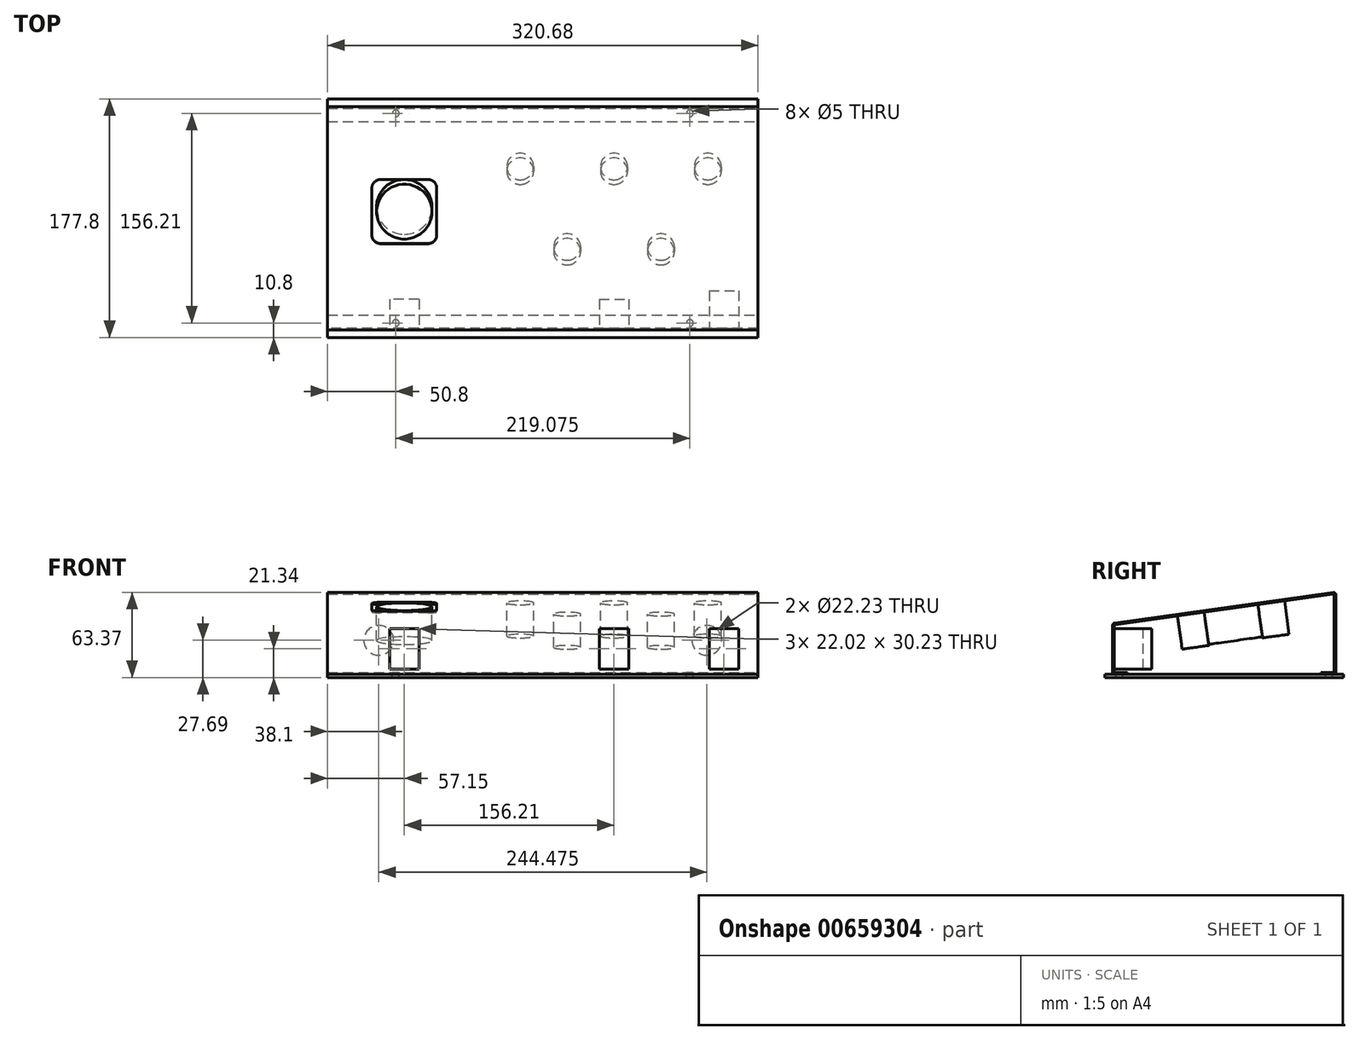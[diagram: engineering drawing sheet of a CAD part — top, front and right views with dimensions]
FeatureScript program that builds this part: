
annotation { "Feature Type Name" : "Feature", "Feature Type Description" : "" }
export const myFeature = defineFeature(function(context is Context, id is Id, definition is map)
    precondition{}
    {
        {
            var Q0;
            Q0=qCreatedBy(makeId("Front.planeOp"),FACE);
            var sketch = newSketch(context, id + "F0", { "sketchPlane" : qUnion([Q0])});
            skLineSegment(sketch, "E0.top", {"start": v(0, 38.1) * mm, "end": v(320.68, 38.1) * mm});
            skLineSegment(sketch, "E0.left", {"start": v(0, 0) * mm, "end": v(0, 38.1) * mm});
            skLineSegment(sketch, "E0.right", {"start": v(320.68, 0) * mm, "end": v(320.68, 38.1) * mm});
            skLineSegment(sketch, "E1", {"start": v(0, 0) * mm, "end": v(0, 0) * mm});
            skLineSegment(sketch, "E2", {"start": v(0, 0) * mm, "end": v(320.68, 0) * mm});
            skPoint(sketch, "E3", {"position": v(0, 19.05) * mm});
            skLineSegment(sketch, "E4.bottom", {"start": v(68.16, 3.94) * mm, "end": v(46.14, 3.94) * mm});
            skLineSegment(sketch, "E4.top", {"start": v(68.16, 34.16) * mm, "end": v(46.14, 34.16) * mm});
            skLineSegment(sketch, "E4.left", {"start": v(68.16, 3.94) * mm, "end": v(68.16, 34.16) * mm});
            skLineSegment(sketch, "E4.right", {"start": v(46.14, 3.94) * mm, "end": v(46.14, 34.16) * mm});
            skPoint(sketch, "E4.middle", {"position": v(57.15, 19.05) * mm});
            skLineSegment(sketch, "E5.bottom", {"start": v(202.35, 3.94) * mm, "end": v(224.37, 3.94) * mm});
            skLineSegment(sketch, "E5.top", {"start": v(202.35, 34.16) * mm, "end": v(224.37, 34.16) * mm});
            skLineSegment(sketch, "E5.left", {"start": v(202.35, 3.94) * mm, "end": v(202.35, 34.16) * mm});
            skLineSegment(sketch, "E5.right", {"start": v(224.37, 3.94) * mm, "end": v(224.37, 34.16) * mm});
            skPoint(sketch, "E5.middle", {"position": v(213.36, 19.05) * mm});
            skLineSegment(sketch, "E6.bottom", {"start": v(284.26, 3.94) * mm, "end": v(306.29, 3.94) * mm});
            skLineSegment(sketch, "E6.top", {"start": v(284.26, 34.16) * mm, "end": v(306.29, 34.16) * mm});
            skLineSegment(sketch, "E6.left", {"start": v(284.26, 3.94) * mm, "end": v(284.26, 34.16) * mm});
            skLineSegment(sketch, "E6.right", {"start": v(306.29, 3.94) * mm, "end": v(306.29, 34.16) * mm});
            skPoint(sketch, "E6.middle", {"position": v(295.28, 19.05) * mm});
            skSolve(sketch);
        }
        {
            var Q0;
            Q0=qCreatedBy(makeId("Right.planeOp"),FACE);
            var sketch = newSketch(context, id + "F1", { "sketchPlane" : qUnion([Q0])});
            skLineSegment(sketch, "E7.0", {"start": v(0, 0) * mm, "end": v(0, 38.1) * mm});
            skLineSegment(sketch, "E8", {"start": v(0, 0) * mm, "end": v(166.37, 0) * mm});
            skLineSegment(sketch, "E9", {"start": v(166.37, 0) * mm, "end": v(166.37, 61.34) * mm});
            skLineSegment(sketch, "E10", {"start": v(166.37, 61.34) * mm, "end": v(0, 38.1) * mm});
            skSolve(sketch);
        }
        {
            var Q0;
            Q0=sQuery(id+"F1.wireOp",EDGE,"E10");
            var Q1;
            Q1=sQuery(id+"F0.wireOp",EDGE,"E0.top");
            cPlane(context, id + "F2", {"entities" : qUnion([Q0, Q1]), "cplaneType" : CPlaneType.LINE_ANGLE, "offset" : 0 * mm, "angle" : 0 * degree, "width" : 152.4 * mm, "height" : 152.4 * mm});
        }
        {
            var Q0;
            Q0=qCreatedBy(id+"F2.planeOp",FACE);
            var sketch = newSketch(context, id + "F3", { "sketchPlane" : qUnion([Q0])});
            skPoint(sketch, "E11.0", {"position": v(320.67, 4.96) * mm});
            skPoint(sketch, "E12.0", {"position": v(0, 5.27) * mm});
            skLineSegment(sketch, "E13.bottom", {"start": v(0, 5.27) * mm, "end": v(320.68, 5.27) * mm});
            skLineSegment(sketch, "E13.top", {"start": v(0, 173.26) * mm, "end": v(320.68, 173.26) * mm});
            skLineSegment(sketch, "E13.left", {"start": v(0, 5.27) * mm, "end": v(0, 173.26) * mm});
            skLineSegment(sketch, "E13.right", {"start": v(320.68, 5.27) * mm, "end": v(320.68, 173.26) * mm});
            skCircle(sketch, "E14", {"center": v(57.15, 94.17) * mm, "radius": 20.64 * mm});
            skCircle(sketch, "E15", {"center": v(39.37, 76.4) * mm, "radius": 1.59 * mm});
            skCircle(sketch, "E16", {"center": v(74.93, 76.4) * mm, "radius": 1.59 * mm});
            skCircle(sketch, "E17", {"center": v(74.93, 111.95) * mm, "radius": 1.59 * mm});
            skCircle(sketch, "E18", {"center": v(39.37, 111.95) * mm, "radius": 1.59 * mm});
            skCircle(sketch, "E19", {"center": v(213.36, 124.42) * mm, "radius": 10 * mm});
            skCircle(sketch, "E20", {"center": v(283.21, 124.42) * mm, "radius": 10 * mm});
            skCircle(sketch, "E21", {"center": v(143.5, 124.42) * mm, "radius": 10 * mm});
            skCircle(sketch, "E22", {"center": v(178.44, 63.93) * mm, "radius": 10 * mm});
            skCircle(sketch, "E23", {"center": v(248.28, 63.93) * mm, "radius": 10 * mm});
            skLineSegment(sketch, "E24", {"start": v(178.44, 63.93) * mm, "end": v(248.28, 63.93) * mm});
            skLineSegment(sketch, "E25", {"start": v(213.36, 124.42) * mm, "end": v(213.36, 63.93) * mm});
            skPoint(sketch, "E26", {"position": v(213.36, 94.17) * mm});
            skLineSegment(sketch, "E27", {"start": v(178.44, 63.93) * mm, "end": v(213.36, 124.42) * mm});
            skLineSegment(sketch, "E28", {"start": v(143.5, 124.42) * mm, "end": v(213.36, 124.42) * mm});
            skLineSegment(sketch, "E29", {"start": v(143.5, 124.42) * mm, "end": v(178.44, 63.93) * mm});
            skLineSegment(sketch, "E30", {"start": v(213.36, 124.42) * mm, "end": v(283.21, 124.42) * mm});
            skLineSegment(sketch, "E31", {"start": v(213.36, 124.42) * mm, "end": v(248.28, 63.93) * mm});
            skLineSegment(sketch, "E32", {"start": v(248.28, 63.93) * mm, "end": v(283.21, 124.42) * mm});
            skPoint(sketch, "E33.0", {"position": v(320.68, 5.27) * mm});
            skPoint(sketch, "E34.0", {"position": v(0, 173.26) * mm});
            skLineSegment(sketch, "E35.bottom", {"start": v(74.93, 118.3) * mm, "end": v(39.37, 118.3) * mm});
            skLineSegment(sketch, "E35.top", {"start": v(74.93, 70.04) * mm, "end": v(39.37, 70.04) * mm});
            skLineSegment(sketch, "E35.left", {"start": v(81.28, 111.95) * mm, "end": v(81.28, 76.4) * mm});
            skLineSegment(sketch, "E35.right", {"start": v(33.02, 111.95) * mm, "end": v(33.02, 76.4) * mm});
            skPoint(sketch, "E36.visualSharp", {"position": v(81.28, 118.3) * mm});
            skArc(sketch, "E36.filletArc", {"start": v(81.28, 111.95) * mm, "mid": v(79.42, 116.44) * mm, "end": v(74.93, 118.3) * mm});
            skPoint(sketch, "E37.visualSharp", {"position": v(33.02, 118.3) * mm});
            skArc(sketch, "E37.filletArc", {"start": v(39.37, 118.3) * mm, "mid": v(34.88, 116.44) * mm, "end": v(33.02, 111.95) * mm});
            skPoint(sketch, "E38.visualSharp", {"position": v(33.02, 70.04) * mm});
            skArc(sketch, "E38.filletArc", {"start": v(33.02, 76.4) * mm, "mid": v(34.88, 71.9) * mm, "end": v(39.37, 70.04) * mm});
            skPoint(sketch, "E39.visualSharp", {"position": v(81.28, 70.04) * mm});
            skArc(sketch, "E39.filletArc", {"start": v(74.93, 70.04) * mm, "mid": v(79.42, 71.9) * mm, "end": v(81.28, 76.4) * mm});
            skSolve(sketch);
        }
        {
            var Q0;
            Q0=sQuery(id+"F0.wireOp",EDGE,"E0.right");
            var Q1;
            Q1=sQuery(id+"F3.wireOp",EDGE,"E13.right");
            cPlane(context, id + "F4", {"entities" : qUnion([Q0, Q1]), "cplaneType" : CPlaneType.LINE_ANGLE, "offset" : 25.4 * mm, "angle" : 0 * degree, "width" : 152.4 * mm, "height" : 152.4 * mm});
        }
        {
            var Q0;
            Q0=qCreatedBy(id+"F4.planeOp",FACE);
            var sketch = newSketch(context, id + "F5", { "sketchPlane" : qUnion([Q0])});
            skLineSegment(sketch, "E40.0", {"start": v(0, 0) * mm, "end": v(0, 38.1) * mm});
            skLineSegment(sketch, "E41.0", {"start": v(0, 0) * mm, "end": v(-166.37, 0) * mm});
            skLineSegment(sketch, "E42.0", {"start": v(-166.37, 0) * mm, "end": v(-166.37, 61.34) * mm});
            skLineSegment(sketch, "E43.0", {"start": v(-166.37, 61.34) * mm, "end": v(0, 38.1) * mm});
            skLineSegment(sketch, "E44", {"start": v(-166.37, 61.34) * mm, "end": v(-166.37, 0) * mm});
            skSolve(sketch);
        }
        {
            var Q0;
            Q0=sQuery(id+"F1.wireOp",EDGE,"E9");
            var Q1;
            Q1=sQuery(id+"F3.wireOp",EDGE,"E13.top");
            cPlane(context, id + "F6", {"entities" : qUnion([Q0, Q1]), "cplaneType" : CPlaneType.LINE_ANGLE, "offset" : 25.4 * mm, "angle" : 0 * degree, "width" : 152.4 * mm, "height" : 152.4 * mm});
        }
        {
            var Q0;
            Q0=qCreatedBy(id+"F6.planeOp",FACE);
            var sketch = newSketch(context, id + "F7", { "sketchPlane" : qUnion([Q0])});
            skLineSegment(sketch, "E45.0", {"start": v(0, 0) * mm, "end": v(0, 61.34) * mm});
            skLineSegment(sketch, "E46.0", {"start": v(0, 61.34) * mm, "end": v(-320.68, 61.34) * mm});
            skLineSegment(sketch, "E47.0", {"start": v(-320.68, 0) * mm, "end": v(-320.68, 61.34) * mm});
            skLineSegment(sketch, "E48", {"start": v(-320.68, 0) * mm, "end": v(0, 0) * mm});
            skCircle(sketch, "E49", {"center": v(-282.58, 25.4) * mm, "radius": 11.11 * mm});
            skCircle(sketch, "E50", {"center": v(-38.1, 25.4) * mm, "radius": 11.11 * mm});
            skSolve(sketch);
        }
        {
            var Q0;
            Q0=qCreatedBy(makeId("Top.planeOp"),FACE);
            var sketch = newSketch(context, id + "F8", { "sketchPlane" : qUnion([Q0])});
            skLineSegment(sketch, "E51.0", {"start": v(0, 0) * mm, "end": v(0, 166.37) * mm});
            skLineSegment(sketch, "E52.0", {"start": v(0, 0) * mm, "end": v(320.68, 0) * mm});
            skLineSegment(sketch, "E53.0", {"start": v(320.68, 0) * mm, "end": v(320.68, 166.37) * mm});
            skLineSegment(sketch, "E54.0", {"start": v(320.68, 166.37) * mm, "end": v(0, 166.37) * mm});
            skCircle(sketch, "E55", {"center": v(50.8, 161.3) * mm, "radius": 2.5 * mm});
            skCircle(sketch, "E56", {"center": v(269.88, 161.3) * mm, "radius": 2.5 * mm});
            skCircle(sketch, "E57", {"center": v(50.8, 5.08) * mm, "radius": 2.5 * mm});
            skCircle(sketch, "E58", {"center": v(269.88, 5.08) * mm, "radius": 2.5 * mm});
            skLineSegment(sketch, "E59", {"start": v(0, 11.11) * mm, "end": v(320.68, 11.11) * mm});
            skLineSegment(sketch, "E60", {"start": v(0, 155.26) * mm, "end": v(320.68, 155.26) * mm});
            skSolve(sketch);
        }
        {
            var Q0;
            Q0=makeQuery(id+"F3.imprint","IMPRINT",FACE,{"disambiguationData":[TD([[makeQuery(id+"F3.imprint","IMPRINT",EDGE,{"derivedFrom":sQuery(id+"F3.wireOp",EDGE,"E13.bottom")}),1.0]])]});
            var Q1;
            {var subQ1=sQuery(id+"F3.wireOp",EDGE,"E19");var subQ7=sQuery(id+"F3.wireOp",EDGE,"E28");var subQ11=makeQuery(id+"F3.imprint","INTERSECT",VERTEX,{"derivedFrom":[subQ1,subQ7]});Q1=makeQuery(id+"F3.imprint","IMPRINT",FACE,{"disambiguationData":[TD([[makeQuery(id+"F3.imprint","IMPRINT",EDGE,{"disambiguationData":[TD([[subQ11,-1.0]])],"derivedFrom":subQ1}),-1.0]])]});}
            var Q2;
            {var subQ3=sQuery(id+"F3.wireOp",EDGE,"E19");var subQ5=sQuery(id+"F3.wireOp",EDGE,"E27");var subQ9=makeQuery(id+"F3.imprint","INTERSECT",VERTEX,{"derivedFrom":[subQ3,subQ5]});Q2=makeQuery(id+"F3.imprint","IMPRINT",FACE,{"disambiguationData":[TD([[makeQuery(id+"F3.imprint","IMPRINT",EDGE,{"disambiguationData":[TD([[subQ9,-1.0]])],"derivedFrom":subQ3}),-1.0]])]});}
            var Q3;
            {var subQ0=sQuery(id+"F3.wireOp",EDGE,"E25");var subQ3=sQuery(id+"F3.wireOp",EDGE,"E19");var subQ4=makeQuery(id+"F3.imprint","INTERSECT",VERTEX,{"derivedFrom":[subQ3,subQ0]});Q3=makeQuery(id+"F3.imprint","IMPRINT",FACE,{"disambiguationData":[TD([[makeQuery(id+"F3.imprint","IMPRINT",EDGE,{"disambiguationData":[TD([[subQ4,-1.0]])],"derivedFrom":subQ3}),-1.0]])]});}
            var Q4;
            {var subQ0=sQuery(id+"F3.wireOp",EDGE,"E30");var subQ1=sQuery(id+"F3.wireOp",EDGE,"E19");var subQ2=makeQuery(id+"F3.imprint","INTERSECT",VERTEX,{"derivedFrom":[subQ1,subQ0]});Q4=makeQuery(id+"F3.imprint","IMPRINT",FACE,{"disambiguationData":[TD([[makeQuery(id+"F3.imprint","IMPRINT",EDGE,{"disambiguationData":[TD([[subQ2,1.0]])],"derivedFrom":subQ1}),-1.0]])]});}
            var Q5;
            Q5=makeQuery(id+"F3.imprint","IMPRINT",FACE,{"disambiguationData":[TD([[makeQuery(id+"F3.imprint","IMPRINT",EDGE,{"derivedFrom":sQuery(id+"F3.wireOp",EDGE,"E14")}),-1.0]])]});
            extrude(context, id + "F9", {"entities" : qUnion([Q0, Q1, Q2, Q3, Q4, Q5]), "oppositeDirection" : true, "depth" : 1.27 * mm, "offsetDistance" : 25.4 * mm});
        }
        {
            var Q0;
            Q0=makeQuery(id+"F0.imprint","IMPRINT",FACE,{"disambiguationData":[TD([[makeQuery(id+"F0.imprint","IMPRINT",EDGE,{"derivedFrom":sQuery(id+"F0.wireOp",EDGE,"E0.top")}),-1.0]])]});
            extrude(context, id + "F10", {"entities" : qUnion([Q0]), "operationType" : NewBodyOperationType.ADD, "oppositeDirection" : true, "depth" : 1.27 * mm, "offsetDistance" : 25.4 * mm});
        }
        {
            var Q0;
            Q0=makeQuery(id+"F7.imprint","IMPRINT",FACE,{"disambiguationData":[TD([[makeQuery(id+"F7.imprint","IMPRINT",EDGE,{"derivedFrom":sQuery(id+"F7.wireOp",EDGE,"E45.0")}),1.0]])]});
            extrude(context, id + "F11", {"entities" : qUnion([Q0]), "operationType" : NewBodyOperationType.ADD, "oppositeDirection" : true, "depth" : 1.27 * mm, "offsetDistance" : 25.4 * mm});
        }
        {
            var Q0;
            Q0=makeQuery(id+"F5.imprint","IMPRINT",FACE,{"disambiguationData":[TD([[makeQuery(id+"F5.imprint","IMPRINT",EDGE,{"derivedFrom":sQuery(id+"F5.wireOp",EDGE,"E43.0")}),-1.0]])]});
            var sketch = newSketch(context, id + "F12", { "sketchPlane" : qUnion([Q0])});
            skLineSegment(sketch, "E61.0", {"start": v(-165.1, 61.34) * mm, "end": v(-166.37, 61.34) * mm});
            skLineSegment(sketch, "E62.0", {"start": v(-165.1, 61.16) * mm, "end": v(-165.1, 61.34) * mm});
            skLineSegment(sketch, "E63.0", {"start": v(-166.55, 60.08) * mm, "end": v(-166.37, 61.34) * mm});
            skLineSegment(sketch, "E64.0", {"start": v(-166.37, 60.06) * mm, "end": v(-166.55, 60.08) * mm});
            skLineSegment(sketch, "E65", {"start": v(-165.1, 61.16) * mm, "end": v(-166.37, 61.34) * mm});
            skLineSegment(sketch, "E66", {"start": v(-166.37, 60.06) * mm, "end": v(-166.37, 61.34) * mm});
            skSolve(sketch);
        }
        {
            var Q0;
            Q0=makeQuery(id+"F12.imprint","IMPRINT",FACE,{"disambiguationData":[TD([[makeQuery(id+"F12.imprint","IMPRINT",EDGE,{"derivedFrom":sQuery(id+"F12.wireOp",EDGE,"E61.0")}),1.0]])]});
            var Q1;
            Q1=makeQuery(id+"F12.imprint","IMPRINT",FACE,{"disambiguationData":[TD([[makeQuery(id+"F12.imprint","IMPRINT",EDGE,{"derivedFrom":sQuery(id+"F12.wireOp",EDGE,"E63.0")}),-1.0]])]});
            extrude(context, id + "F13", {"entities" : qUnion([Q0, Q1]), "operationType" : NewBodyOperationType.REMOVE, "endBound" : BoundingType.THROUGH_ALL, "depth" : 25.4 * mm, "offsetDistance" : 25.4 * mm});
        }
        {
            var Q0;
            {var subQ1=sQuery(id+"F8.wireOp",EDGE,"E52.0");Q0=makeQuery(id+"F8.imprint","IMPRINT",FACE,{"disambiguationData":[TD([[makeQuery(id+"F8.imprint","IMPRINT",EDGE,{"derivedFrom":subQ1}),1.0]])]});}
            var Q1;
            {var subQ0=sQuery(id+"F8.wireOp",EDGE,"E54.0");Q1=makeQuery(id+"F8.imprint","IMPRINT",FACE,{"disambiguationData":[TD([[makeQuery(id+"F8.imprint","IMPRINT",EDGE,{"derivedFrom":subQ0}),1.0]])]});}
            extrude(context, id + "F14", {"entities" : qUnion([Q0, Q1]), "operationType" : NewBodyOperationType.ADD, "depth" : 1.27 * mm, "offsetDistance" : 25.4 * mm});
        }
        {
            var Q0;
            Q0=makeQuery(id+"F10.boolean.opBoolean","MERGE",EDGE,{"derivedFrom":[makeQuery(id+"F9.opExtrude","CAP_EDGE",EDGE,{"disambiguationData":[OSD([sQuery(id+"F3.wireOp",EDGE,"E13.bottom")])],"isStart":true}),makeQuery(id+"F10.opExtrude","CAP_EDGE",EDGE,{"disambiguationData":[OSD([sQuery(id+"F0.wireOp",EDGE,"E0.top")])],"isStart":true})]});
            var Q1;
            {var subQ0=sQuery(id+"F12.wireOp",EDGE,"E66");var subQ1=sQuery(id+"F12.wireOp",EDGE,"E65");var subQ2=sQuery(id+"F12.wireOp",EDGE,"E63.0");var subQ3=sQuery(id+"F12.wireOp",EDGE,"E61.0");Q1=makeQuery(id+"F13.boolean.opBoolean","MERGE",EDGE,{"derivedFrom":[makeQuery(id+"F11.boolean.opBoolean","MERGE",EDGE,{"derivedFrom":[makeQuery(id+"F9.opExtrude","CAP_EDGE",EDGE,{"disambiguationData":[OSD([sQuery(id+"F3.wireOp",EDGE,"E13.top")])],"isStart":true}),makeQuery(id+"F11.opExtrude","CAP_EDGE",EDGE,{"disambiguationData":[OSD([sQuery(id+"F7.wireOp",EDGE,"E46.0")])],"isStart":true})]}),makeQuery(id+"F13.opExtrude","SWEPT_EDGE",EDGE,{"disambiguationData":[OSD([subQ3,subQ2,subQ1,subQ0]),OD(0.0)]}),makeQuery(id+"F13.opExtrude","SWEPT_EDGE",EDGE,{"disambiguationData":[OSD([subQ3,subQ2,subQ1,subQ0]),OD(1.0)]})]});}
            var Q2;
            Q2=makeQuery(id+"F11.opExtrude","CAP_EDGE",EDGE,{"disambiguationData":[OSD([sQuery(id+"F7.wireOp",EDGE,"E48")])],"isStart":true});
            var Q3;
            Q3=makeQuery(id+"F10.opExtrude","CAP_EDGE",EDGE,{"disambiguationData":[OSD([sQuery(id+"F0.wireOp",EDGE,"E2")])],"isStart":true});
            fillet(context, id + "F15", {"entities" : qUnion([Q0, Q1, Q2, Q3]), "radius" : 1.78 * mm, "tangentPropagation" : true, "allowEdgeOverflow" : false});
        }
        {
            var Q0;
            Q0=makeQuery(id+"F11.boolean.opBoolean","INTERSECT",EDGE,{"derivedFrom":[makeQuery(id+"F9.opExtrude","CAP_FACE",FACE,{"disambiguationData":[OSD([sQuery(id+"F3.wireOp",EDGE,"E13.bottom"),sQuery(id+"F3.wireOp",EDGE,"E13.top"),sQuery(id+"F3.wireOp",EDGE,"E13.left"),sQuery(id+"F3.wireOp",EDGE,"E13.right"),sQuery(id+"F3.wireOp",EDGE,"E14"),sQuery(id+"F3.wireOp",EDGE,"E15"),sQuery(id+"F3.wireOp",EDGE,"E16"),sQuery(id+"F3.wireOp",EDGE,"E17"),sQuery(id+"F3.wireOp",EDGE,"E18"),sQuery(id+"F3.wireOp",EDGE,"E19"),sQuery(id+"F3.wireOp",EDGE,"E20"),sQuery(id+"F3.wireOp",EDGE,"E21"),sQuery(id+"F3.wireOp",EDGE,"E22"),sQuery(id+"F3.wireOp",EDGE,"E23")])],"isStart":false}),makeQuery(id+"F11.opExtrude","CAP_FACE",FACE,{"disambiguationData":[OSD([sQuery(id+"F7.wireOp",EDGE,"E45.0"),sQuery(id+"F7.wireOp",EDGE,"E46.0"),sQuery(id+"F7.wireOp",EDGE,"E47.0"),sQuery(id+"F7.wireOp",EDGE,"E48"),sQuery(id+"F7.wireOp",EDGE,"E49"),sQuery(id+"F7.wireOp",EDGE,"E50")])],"isStart":false})]});
            var Q1;
            Q1=makeQuery(id+"F10.boolean.opBoolean","INTERSECT",EDGE,{"derivedFrom":[makeQuery(id+"F9.opExtrude","CAP_FACE",FACE,{"disambiguationData":[OSD([sQuery(id+"F3.wireOp",EDGE,"E13.bottom"),sQuery(id+"F3.wireOp",EDGE,"E13.top"),sQuery(id+"F3.wireOp",EDGE,"E13.left"),sQuery(id+"F3.wireOp",EDGE,"E13.right"),sQuery(id+"F3.wireOp",EDGE,"E14"),sQuery(id+"F3.wireOp",EDGE,"E15"),sQuery(id+"F3.wireOp",EDGE,"E16"),sQuery(id+"F3.wireOp",EDGE,"E17"),sQuery(id+"F3.wireOp",EDGE,"E18"),sQuery(id+"F3.wireOp",EDGE,"E19"),sQuery(id+"F3.wireOp",EDGE,"E20"),sQuery(id+"F3.wireOp",EDGE,"E21"),sQuery(id+"F3.wireOp",EDGE,"E22"),sQuery(id+"F3.wireOp",EDGE,"E23")])],"isStart":false}),makeQuery(id+"F10.opExtrude","CAP_FACE",FACE,{"disambiguationData":[OSD([sQuery(id+"F0.wireOp",EDGE,"E0.top"),sQuery(id+"F0.wireOp",EDGE,"E0.left"),sQuery(id+"F0.wireOp",EDGE,"E0.right"),sQuery(id+"F0.wireOp",EDGE,"E2"),sQuery(id+"F0.wireOp",EDGE,"E4.bottom"),sQuery(id+"F0.wireOp",EDGE,"E4.top"),sQuery(id+"F0.wireOp",EDGE,"E4.left"),sQuery(id+"F0.wireOp",EDGE,"E4.right"),sQuery(id+"F0.wireOp",EDGE,"E5.bottom"),sQuery(id+"F0.wireOp",EDGE,"E5.top"),sQuery(id+"F0.wireOp",EDGE,"E5.left"),sQuery(id+"F0.wireOp",EDGE,"E5.right"),sQuery(id+"F0.wireOp",EDGE,"E6.bottom"),sQuery(id+"F0.wireOp",EDGE,"E6.top"),sQuery(id+"F0.wireOp",EDGE,"E6.left"),sQuery(id+"F0.wireOp",EDGE,"E6.right")])],"isStart":false})]});
            var Q2;
            Q2=makeQuery(id+"F14.boolean.opBoolean","INTERSECT",EDGE,{"derivedFrom":[makeQuery(id+"F10.opExtrude","CAP_FACE",FACE,{"disambiguationData":[OSD([sQuery(id+"F0.wireOp",EDGE,"E0.top"),sQuery(id+"F0.wireOp",EDGE,"E0.left"),sQuery(id+"F0.wireOp",EDGE,"E0.right"),sQuery(id+"F0.wireOp",EDGE,"E2"),sQuery(id+"F0.wireOp",EDGE,"E4.bottom"),sQuery(id+"F0.wireOp",EDGE,"E4.top"),sQuery(id+"F0.wireOp",EDGE,"E4.left"),sQuery(id+"F0.wireOp",EDGE,"E4.right"),sQuery(id+"F0.wireOp",EDGE,"E5.bottom"),sQuery(id+"F0.wireOp",EDGE,"E5.top"),sQuery(id+"F0.wireOp",EDGE,"E5.left"),sQuery(id+"F0.wireOp",EDGE,"E5.right"),sQuery(id+"F0.wireOp",EDGE,"E6.bottom"),sQuery(id+"F0.wireOp",EDGE,"E6.top"),sQuery(id+"F0.wireOp",EDGE,"E6.left"),sQuery(id+"F0.wireOp",EDGE,"E6.right")])],"isStart":false}),makeQuery(id+"F14.opExtrude","CAP_FACE",FACE,{"disambiguationData":[OSD([sQuery(id+"F8.wireOp",EDGE,"E51.0"),sQuery(id+"F8.wireOp",EDGE,"E52.0"),sQuery(id+"F8.wireOp",EDGE,"E53.0"),sQuery(id+"F8.wireOp",EDGE,"E57"),sQuery(id+"F8.wireOp",EDGE,"E58"),sQuery(id+"F8.wireOp",EDGE,"E59")])],"isStart":false})]});
            var Q3;
            {var subQ1=sQuery(id+"F7.wireOp",EDGE,"E47.0");var subQ2=sQuery(id+"F7.wireOp",EDGE,"E49");var subQ4=sQuery(id+"F7.wireOp",EDGE,"E50");var subQ5=sQuery(id+"F7.wireOp",EDGE,"E45.0");var subQ6=sQuery(id+"F7.wireOp",EDGE,"E48");Q3=makeQuery(id+"F14.boolean.opBoolean","INTERSECT",EDGE,{"derivedFrom":[makeQuery(id+"F11.boolean.opBoolean","SPLIT",FACE,{"disambiguationData":[TD([makeQuery(id+"F11.opExtrude","SWEPT_FACE",FACE,{"disambiguationData":[OSD([subQ6])]})])],"derivedFrom":makeQuery(id+"F11.opExtrude","CAP_FACE",FACE,{"disambiguationData":[OSD([subQ5,sQuery(id+"F7.wireOp",EDGE,"E46.0"),subQ1,subQ6,subQ2,subQ4])],"isStart":false})}),makeQuery(id+"F14.opExtrude","CAP_FACE",FACE,{"disambiguationData":[OSD([sQuery(id+"F8.wireOp",EDGE,"E51.0"),sQuery(id+"F8.wireOp",EDGE,"E53.0"),sQuery(id+"F8.wireOp",EDGE,"E54.0"),sQuery(id+"F8.wireOp",EDGE,"E55"),sQuery(id+"F8.wireOp",EDGE,"E56"),sQuery(id+"F8.wireOp",EDGE,"E60")])],"isStart":false})]});}
            fillet(context, id + "F16", {"entities" : qUnion([Q0, Q1, Q2, Q3]), "radius" : 0.76 * mm, "tangentPropagation" : true, "allowEdgeOverflow" : false});
        }
        {
            var Q0;
            Q0=makeQuery(id+"F3.imprint","IMPRINT",FACE,{"disambiguationData":[TD([[makeQuery(id+"F3.imprint","IMPRINT",EDGE,{"derivedFrom":sQuery(id+"F3.wireOp",EDGE,"E14")}),1.0]])]});
            var Q1;
            Q1=sQuery(id+"F3.wireOp",EDGE,"E14");
            extrude(context, id + "F17", {"entities" : qUnion([Q0]), "surfaceEntities" : qUnion([Q1]), "oppositeDirection" : true, "depth" : 25.43 * mm, "offsetDistance" : 25.4 * mm});
        }
        {
            var Q0;
            Q0=makeQuery(id+"F3.imprint","IMPRINT",FACE,{"disambiguationData":[TD([[makeQuery(id+"F3.imprint","IMPRINT",EDGE,{"derivedFrom":sQuery(id+"F3.wireOp",EDGE,"E14")}),-1.0]])]});
            extrude(context, id + "F18", {"entities" : qUnion([Q0]), "operationType" : NewBodyOperationType.ADD, "oppositeDirection" : true, "depth" : 8.38 * mm, "offsetDistance" : 25.4 * mm});
        }
        {
            var Q0;
            {var subQ0=sQuery(id+"F3.wireOp",EDGE,"E30");var subQ1=sQuery(id+"F3.wireOp",EDGE,"E20");var subQ2=makeQuery(id+"F3.imprint","INTERSECT",VERTEX,{"derivedFrom":[subQ1,subQ0]});Q0=makeQuery(id+"F3.imprint","IMPRINT",FACE,{"disambiguationData":[TD([[makeQuery(id+"F3.imprint","IMPRINT",EDGE,{"disambiguationData":[TD([[subQ2,1.0]])],"derivedFrom":subQ1}),1.0]])]});}
            var Q1;
            {var subQ0=sQuery(id+"F3.wireOp",EDGE,"E30");var subQ1=sQuery(id+"F3.wireOp",EDGE,"E20");var subQ2=makeQuery(id+"F3.imprint","INTERSECT",VERTEX,{"derivedFrom":[subQ1,subQ0]});Q1=makeQuery(id+"F3.imprint","IMPRINT",FACE,{"disambiguationData":[TD([[makeQuery(id+"F3.imprint","IMPRINT",EDGE,{"disambiguationData":[TD([[subQ2,-1.0]])],"derivedFrom":subQ1}),1.0]])]});}
            var Q2;
            {var subQ0=sQuery(id+"F3.wireOp",EDGE,"E30");var subQ1=sQuery(id+"F3.wireOp",EDGE,"E19");var subQ2=makeQuery(id+"F3.imprint","INTERSECT",VERTEX,{"derivedFrom":[subQ1,subQ0]});Q2=makeQuery(id+"F3.imprint","IMPRINT",FACE,{"disambiguationData":[TD([[makeQuery(id+"F3.imprint","IMPRINT",EDGE,{"disambiguationData":[TD([[subQ2,1.0]])],"derivedFrom":subQ1}),1.0]])]});}
            var Q3;
            {var subQ0=sQuery(id+"F3.wireOp",EDGE,"E25");var subQ1=sQuery(id+"F3.wireOp",EDGE,"E19");var subQ2=makeQuery(id+"F3.imprint","INTERSECT",VERTEX,{"derivedFrom":[subQ1,subQ0]});Q3=makeQuery(id+"F3.imprint","IMPRINT",FACE,{"disambiguationData":[TD([[makeQuery(id+"F3.imprint","IMPRINT",EDGE,{"disambiguationData":[TD([[subQ2,-1.0]])],"derivedFrom":subQ1}),1.0]])]});}
            var Q4;
            {var subQ0=sQuery(id+"F3.wireOp",EDGE,"E27");var subQ1=sQuery(id+"F3.wireOp",EDGE,"E19");var subQ2=makeQuery(id+"F3.imprint","INTERSECT",VERTEX,{"derivedFrom":[subQ1,subQ0]});Q4=makeQuery(id+"F3.imprint","IMPRINT",FACE,{"disambiguationData":[TD([[makeQuery(id+"F3.imprint","IMPRINT",EDGE,{"disambiguationData":[TD([[subQ2,-1.0]])],"derivedFrom":subQ1}),1.0]])]});}
            var Q5;
            {var subQ0=sQuery(id+"F3.wireOp",EDGE,"E28");var subQ1=sQuery(id+"F3.wireOp",EDGE,"E19");var subQ2=makeQuery(id+"F3.imprint","INTERSECT",VERTEX,{"derivedFrom":[subQ1,subQ0]});Q5=makeQuery(id+"F3.imprint","IMPRINT",FACE,{"disambiguationData":[TD([[makeQuery(id+"F3.imprint","IMPRINT",EDGE,{"disambiguationData":[TD([[subQ2,-1.0]])],"derivedFrom":subQ1}),1.0]])]});}
            var Q6;
            {var subQ0=sQuery(id+"F3.wireOp",EDGE,"E28");var subQ1=sQuery(id+"F3.wireOp",EDGE,"E19");var subQ2=makeQuery(id+"F3.imprint","INTERSECT",VERTEX,{"derivedFrom":[subQ1,subQ0]});Q6=makeQuery(id+"F3.imprint","IMPRINT",FACE,{"disambiguationData":[TD([[makeQuery(id+"F3.imprint","IMPRINT",EDGE,{"disambiguationData":[TD([[subQ2,1.0]])],"derivedFrom":subQ1}),1.0]])]});}
            var Q7;
            {var subQ0=sQuery(id+"F3.wireOp",EDGE,"E28");var subQ1=sQuery(id+"F3.wireOp",EDGE,"E21");var subQ2=makeQuery(id+"F3.imprint","INTERSECT",VERTEX,{"derivedFrom":[subQ1,subQ0]});Q7=makeQuery(id+"F3.imprint","IMPRINT",FACE,{"disambiguationData":[TD([[makeQuery(id+"F3.imprint","IMPRINT",EDGE,{"disambiguationData":[TD([[subQ2,-1.0]])],"derivedFrom":subQ1}),1.0]])]});}
            var Q8;
            {var subQ0=sQuery(id+"F3.wireOp",EDGE,"E28");var subQ1=sQuery(id+"F3.wireOp",EDGE,"E21");var subQ2=makeQuery(id+"F3.imprint","INTERSECT",VERTEX,{"derivedFrom":[subQ1,subQ0]});Q8=makeQuery(id+"F3.imprint","IMPRINT",FACE,{"disambiguationData":[TD([[makeQuery(id+"F3.imprint","IMPRINT",EDGE,{"disambiguationData":[TD([[subQ2,1.0]])],"derivedFrom":subQ1}),1.0]])]});}
            var Q9;
            {var subQ0=sQuery(id+"F3.wireOp",EDGE,"E27");var subQ1=sQuery(id+"F3.wireOp",EDGE,"E22");var subQ2=makeQuery(id+"F3.imprint","INTERSECT",VERTEX,{"derivedFrom":[subQ1,subQ0]});Q9=makeQuery(id+"F3.imprint","IMPRINT",FACE,{"disambiguationData":[TD([[makeQuery(id+"F3.imprint","IMPRINT",EDGE,{"disambiguationData":[TD([[subQ2,-1.0]])],"derivedFrom":subQ1}),1.0]])]});}
            var Q10;
            {var subQ0=sQuery(id+"F3.wireOp",EDGE,"E27");var subQ1=sQuery(id+"F3.wireOp",EDGE,"E22");var subQ2=makeQuery(id+"F3.imprint","INTERSECT",VERTEX,{"derivedFrom":[subQ1,subQ0]});Q10=makeQuery(id+"F3.imprint","IMPRINT",FACE,{"disambiguationData":[TD([[makeQuery(id+"F3.imprint","IMPRINT",EDGE,{"disambiguationData":[TD([[subQ2,1.0]])],"derivedFrom":subQ1}),1.0]])]});}
            var Q11;
            {var subQ0=sQuery(id+"F3.wireOp",EDGE,"E24");var subQ1=sQuery(id+"F3.wireOp",EDGE,"E22");var subQ2=makeQuery(id+"F3.imprint","INTERSECT",VERTEX,{"derivedFrom":[subQ1,subQ0]});Q11=makeQuery(id+"F3.imprint","IMPRINT",FACE,{"disambiguationData":[TD([[makeQuery(id+"F3.imprint","IMPRINT",EDGE,{"disambiguationData":[TD([[subQ2,1.0]])],"derivedFrom":subQ1}),1.0]])]});}
            var Q12;
            {var subQ0=sQuery(id+"F3.wireOp",EDGE,"E31");var subQ1=sQuery(id+"F3.wireOp",EDGE,"E23");var subQ2=makeQuery(id+"F3.imprint","INTERSECT",VERTEX,{"derivedFrom":[subQ1,subQ0]});Q12=makeQuery(id+"F3.imprint","IMPRINT",FACE,{"disambiguationData":[TD([[makeQuery(id+"F3.imprint","IMPRINT",EDGE,{"disambiguationData":[TD([[subQ2,1.0]])],"derivedFrom":subQ1}),1.0]])]});}
            var Q13;
            {var subQ0=sQuery(id+"F3.wireOp",EDGE,"E31");var subQ1=sQuery(id+"F3.wireOp",EDGE,"E23");var subQ2=makeQuery(id+"F3.imprint","INTERSECT",VERTEX,{"derivedFrom":[subQ1,subQ0]});Q13=makeQuery(id+"F3.imprint","IMPRINT",FACE,{"disambiguationData":[TD([[makeQuery(id+"F3.imprint","IMPRINT",EDGE,{"disambiguationData":[TD([[subQ2,-1.0]])],"derivedFrom":subQ1}),1.0]])]});}
            var Q14;
            {var subQ0=sQuery(id+"F3.wireOp",EDGE,"E32");var subQ1=sQuery(id+"F3.wireOp",EDGE,"E23");var subQ2=makeQuery(id+"F3.imprint","INTERSECT",VERTEX,{"derivedFrom":[subQ1,subQ0]});Q14=makeQuery(id+"F3.imprint","IMPRINT",FACE,{"disambiguationData":[TD([[makeQuery(id+"F3.imprint","IMPRINT",EDGE,{"disambiguationData":[TD([[subQ2,1.0]])],"derivedFrom":subQ1}),1.0]])]});}
            var Q15;
            Q15=sQuery(id+"F3.wireOp",EDGE,"E21");
            var Q16;
            Q16=sQuery(id+"F3.wireOp",EDGE,"E22");
            var Q17;
            Q17=sQuery(id+"F3.wireOp",EDGE,"E19");
            var Q18;
            Q18=sQuery(id+"F3.wireOp",EDGE,"E23");
            var Q19;
            Q19=sQuery(id+"F3.wireOp",EDGE,"E20");
            extrude(context, id + "F19", {"entities" : qUnion([Q0, Q1, Q2, Q3, Q4, Q5, Q6, Q7, Q8, Q9, Q10, Q11, Q12, Q13, Q14]), "operationType" : NewBodyOperationType.ADD, "surfaceEntities" : qUnion([Q15, Q16, Q17, Q18, Q19]), "oppositeDirection" : true, "depth" : 25 * mm + 1.27 * mm, "offsetDistance" : 25.4 * mm});
        }
        {
            var Q0;
            Q0=makeQuery(id+"F14.boolean.opBoolean","MERGE",FACE,{"derivedFrom":[makeQuery(id+"F11.opExtrude","SWEPT_FACE",FACE,{"disambiguationData":[OSD([sQuery(id+"F7.wireOp",EDGE,"E48")])]}),makeQuery(id+"F14.opExtrude","CAP_FACE",FACE,{"disambiguationData":[OSD([sQuery(id+"F8.wireOp",EDGE,"E51.0"),sQuery(id+"F8.wireOp",EDGE,"E53.0"),sQuery(id+"F8.wireOp",EDGE,"E54.0"),sQuery(id+"F8.wireOp",EDGE,"E55"),sQuery(id+"F8.wireOp",EDGE,"E56"),sQuery(id+"F8.wireOp",EDGE,"E60")])],"isStart":true})]});
            var sketch = newSketch(context, id + "F20", { "sketchPlane" : qUnion([Q0])});
            skCircle(sketch, "E67.0", {"center": v(50.8, -161.3) * mm, "radius": 2.5 * mm});
            skCircle(sketch, "E68.0", {"center": v(50.8, -5.08) * mm, "radius": 2.5 * mm});
            skCircle(sketch, "E69.0", {"center": v(269.88, -5.08) * mm, "radius": 2.5 * mm});
            skCircle(sketch, "E70.0", {"center": v(269.88, -161.3) * mm, "radius": 2.5 * mm});
            skPoint(sketch, "E71.0", {"position": v(0, -159.92) * mm});
            skLineSegment(sketch, "E72.0", {"start": v(0, -155.26) * mm, "end": v(0, -164.6) * mm});
            skLineSegment(sketch, "E73.0", {"start": v(0, -11.11) * mm, "end": v(0, -1.78) * mm});
            skLineSegment(sketch, "E74.0", {"start": v(320.68, -11.11) * mm, "end": v(320.68, -1.78) * mm});
            skLineSegment(sketch, "E75.0", {"start": v(320.68, -155.26) * mm, "end": v(320.68, -164.6) * mm});
            skLineSegment(sketch, "E76", {"start": v(0, -155.26) * mm, "end": v(0, -11.11) * mm});
            skLineSegment(sketch, "E77", {"start": v(320.68, -11.11) * mm, "end": v(320.68, -155.26) * mm});
            skLineSegment(sketch, "E78", {"start": v(320.68, -164.6) * mm, "end": v(320.68, -172.09) * mm});
            skLineSegment(sketch, "E79", {"start": v(320.68, -172.09) * mm, "end": v(0, -172.09) * mm});
            skLineSegment(sketch, "E80", {"start": v(0, -172.09) * mm, "end": v(0, -164.6) * mm});
            skLineSegment(sketch, "E81", {"start": v(0, -1.78) * mm, "end": v(0, 5.71) * mm});
            skLineSegment(sketch, "E82", {"start": v(0, 5.71) * mm, "end": v(320.68, 5.71) * mm});
            skLineSegment(sketch, "E83", {"start": v(320.68, 5.72) * mm, "end": v(320.68, -1.78) * mm});
            skSolve(sketch);
        }
        {
            var Q0;
            Q0=makeQuery(id+"F20.imprint","IMPRINT",FACE,{"disambiguationData":[TD([[makeQuery(id+"F20.imprint","IMPRINT",EDGE,{"derivedFrom":sQuery(id+"F20.wireOp",EDGE,"E78")}),-1.0]])]});
            var Q1;
            Q1=makeQuery(id+"F20.imprint","IMPRINT",FACE,{"disambiguationData":[TD([[makeQuery(id+"F20.imprint","IMPRINT",EDGE,{"derivedFrom":sQuery(id+"F20.wireOp",EDGE,"E67.0")}),1.0]])]});
            var Q2;
            Q2=makeQuery(id+"F20.imprint","IMPRINT",FACE,{"disambiguationData":[TD([[makeQuery(id+"F20.imprint","IMPRINT",EDGE,{"derivedFrom":sQuery(id+"F20.wireOp",EDGE,"E68.0")}),-1.0]])]});
            extrude(context, id + "F21", {"entities" : qUnion([Q0, Q1, Q2]), "depth" : 2.3 * mm, "offsetDistance" : 25.4 * mm});
        }
        {
            var Q0;
            Q0=makeQuery(id+"F3.imprint","IMPRINT",FACE,{"disambiguationData":[TD([[makeQuery(id+"F3.imprint","IMPRINT",EDGE,{"derivedFrom":sQuery(id+"F3.wireOp",EDGE,"E14")}),-1.0]])]});
            extrude(context, id + "F22", {"entities" : qUnion([Q0]), "operationType" : NewBodyOperationType.REMOVE, "endBound" : BoundingType.UP_TO_NEXT, "oppositeDirection" : true, "depth" : 25.4 * mm, "offsetDistance" : 25.4 * mm});
        }
        {
            var Q0;
            Q0=makeQuery(id+"F0.imprint","IMPRINT",FACE,{"disambiguationData":[TD([[makeQuery(id+"F0.imprint","IMPRINT",EDGE,{"derivedFrom":sQuery(id+"F0.wireOp",EDGE,"E4.bottom")}),-1.0]])]});
            var Q1;
            Q1=makeQuery(id+"F0.imprint","IMPRINT",FACE,{"disambiguationData":[TD([[makeQuery(id+"F0.imprint","IMPRINT",EDGE,{"derivedFrom":sQuery(id+"F0.wireOp",EDGE,"E5.bottom")}),1.0]])]});
            extrude(context, id + "F23", {"entities" : qUnion([Q0, Q1]), "oppositeDirection" : true, "depth" : 22.68 * mm, "offsetDistance" : 25.4 * mm});
        }
        {
            var Q0;
            Q0=makeQuery(id+"F0.imprint","IMPRINT",FACE,{"disambiguationData":[TD([[makeQuery(id+"F0.imprint","IMPRINT",EDGE,{"derivedFrom":sQuery(id+"F0.wireOp",EDGE,"E6.bottom")}),1.0]])]});
            extrude(context, id + "F24", {"entities" : qUnion([Q0]), "oppositeDirection" : true, "depth" : 29 * mm, "offsetDistance" : 25.4 * mm});
        }
    });
